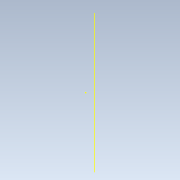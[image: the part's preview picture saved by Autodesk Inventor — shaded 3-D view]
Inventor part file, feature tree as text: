
AUTODESK INVENTOR PART (.ipt)
format: ipt  version: 2021 (Build 250183000, 183)  size: 105,472 bytes
history: native  units: mm
features: other x4, revolve x1, sketch x1, reference x1
ambient origin geometry x8: Origin, YZ Plane, XZ Plane, XY Plane, X Axis, Y Axis, Z Axis, Center Point
bodies: Body1 (feature_tree)
feature tree (7):
  other  "Sólido1"
  revolve  "Revolución1"  [1 undecoded]
  sketch  "Boceto2"  dims[d0=1.0mm d1=20.0mm d2=20.0mm d3=90.0deg]
  reference  "Referencia4"
  parser-record x1  (decoder bookkeeping rows leaked as tree rows — omitted from the tree; the rows remain in map.json)
  other  "Ensamble_Llanta.iam"
  other  "cubierta:1"
note: 1 file-system path scrubbed to <path> (originals preserved in map.json)
note: 1 required parameter value undecoded (feature->parameter linkage not recoverable at this tier; creation-order binding heuristic only, values carry confidence <= 0.55)
